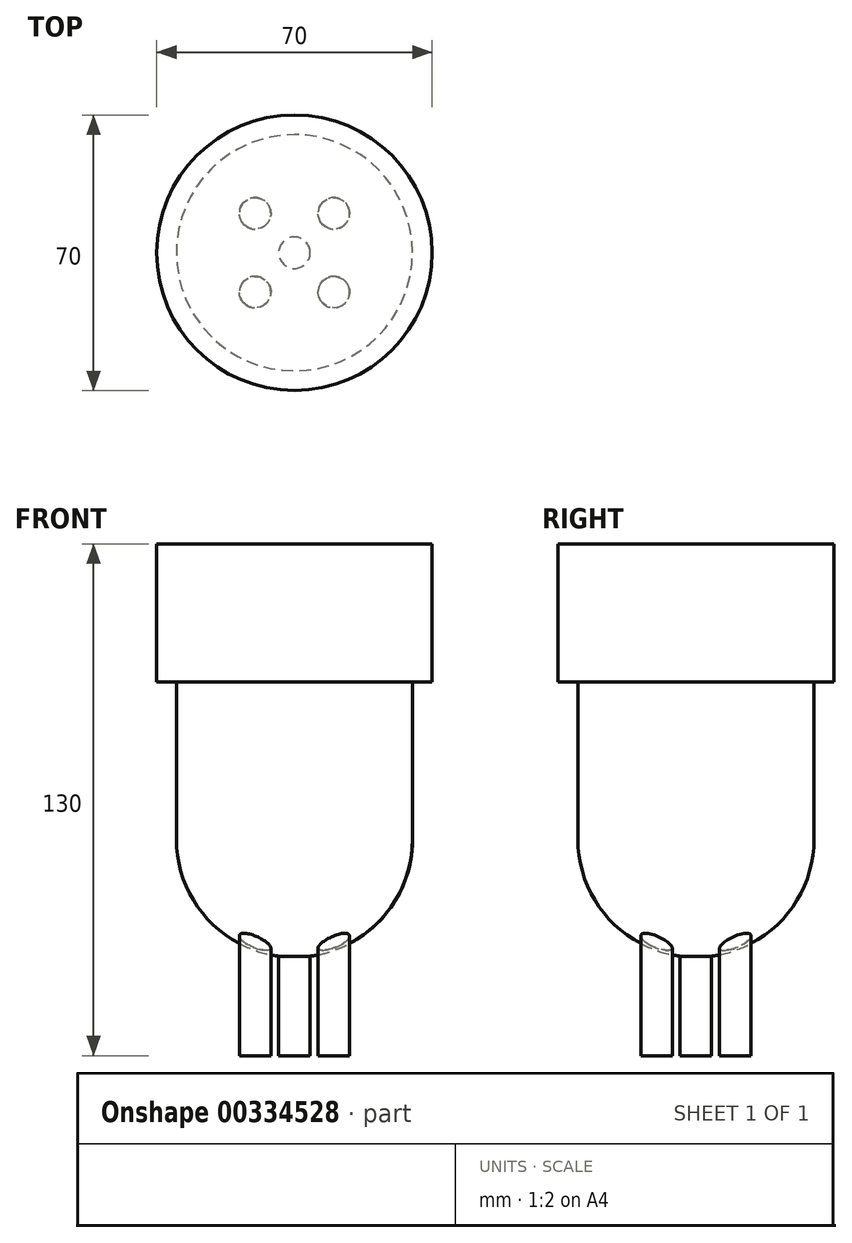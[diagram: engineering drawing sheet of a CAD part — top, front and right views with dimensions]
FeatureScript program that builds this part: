
annotation { "Feature Type Name" : "Feature", "Feature Type Description" : "" }
export const myFeature = defineFeature(function(context is Context, id is Id, definition is map)
    precondition{}
    {
        {
            var Q0;
            Q0=qCreatedBy(makeId("Front.planeOp"),FACE);
            var sketch = newSketch(context, id + "F0", { "sketchPlane" : qUnion([Q0])});
            skLineSegment(sketch, "E0.bottom", {"start": v(0, 70) * mm, "end": v(30, 70) * mm});
            skLineSegment(sketch, "E0.top", {"start": v(0, 30) * mm, "end": v(30, 30) * mm});
            skLineSegment(sketch, "E0.left", {"start": v(0, 70) * mm, "end": v(0, 30) * mm});
            skLineSegment(sketch, "E0.right", {"start": v(30, 70) * mm, "end": v(30, 30) * mm});
            skArc(sketch, "E1", {"start": v(30, 30) * mm, "mid": v(21.21, 8.79) * mm, "end": v(0, 0) * mm});
            skLineSegment(sketch, "E2", {"start": v(0, 30) * mm, "end": v(0, 0) * mm});
            skLineSegment(sketch, "E3.bottom", {"start": v(0, 70) * mm, "end": v(35, 70) * mm});
            skLineSegment(sketch, "E3.top", {"start": v(0, 105) * mm, "end": v(35, 105) * mm});
            skLineSegment(sketch, "E3.left", {"start": v(0, 70) * mm, "end": v(0, 105) * mm});
            skLineSegment(sketch, "E3.right", {"start": v(35, 70) * mm, "end": v(35, 105) * mm});
            skLineSegment(sketch, "E4", {"start": v(0, 70) * mm, "end": v(-15.84, 70) * mm, "construction": true});
            skLineSegment(sketch, "E5", {"start": v(0, 0) * mm, "end": v(0, -28.93) * mm, "construction": true});
            skSolve(sketch);
        }
        {
            var Q0;
            Q0=makeQuery(id+"F0.imprint","IMPRINT",FACE,{"disambiguationData":[TD([[makeQuery(id+"F0.imprint","IMPRINT",EDGE,{"derivedFrom":sQuery(id+"F0.wireOp",EDGE,"E3.top")}),-1.0]])]});
            var Q1;
            Q1=makeQuery(id+"F0.imprint","IMPRINT",FACE,{"disambiguationData":[TD([[makeQuery(id+"F0.imprint","IMPRINT",EDGE,{"derivedFrom":sQuery(id+"F0.wireOp",EDGE,"E0.top")}),1.0]])]});
            var Q2;
            Q2=makeQuery(id+"F0.imprint","IMPRINT",FACE,{"disambiguationData":[TD([[makeQuery(id+"F0.imprint","IMPRINT",EDGE,{"derivedFrom":sQuery(id+"F0.wireOp",EDGE,"E0.top")}),-1.0]])]});
            var Q3;
            Q3=sQuery(id+"F0.wireOp",EDGE,"E0.left");
            revolve(context, id + "F1", {"entities" : qUnion([Q0, Q1, Q2]), "axis" : qUnion([Q3]), "revolveType" : RevolveType.FULL});
        }
        {
            var Q0;
            Q0=qCreatedBy(makeId("Top.planeOp"),FACE);
            var sketch = newSketch(context, id + "F2", { "sketchPlane" : qUnion([Q0])});
            skLineSegment(sketch, "E6.bottom", {"start": v(10, 10) * mm, "end": v(-10, 10) * mm});
            skLineSegment(sketch, "E6.top", {"start": v(10, -10) * mm, "end": v(-10, -10) * mm});
            skLineSegment(sketch, "E6.left", {"start": v(10, 10) * mm, "end": v(10, -10) * mm});
            skLineSegment(sketch, "E6.right", {"start": v(-10, 10) * mm, "end": v(-10, -10) * mm});
            skPoint(sketch, "E6.middle", {"position": v(0, 0) * mm});
            skCircle(sketch, "E7", {"center": v(0, 0) * mm, "radius": 4 * mm});
            skCircle(sketch, "E8", {"center": v(10, -10) * mm, "radius": 4 * mm});
            skCircle(sketch, "E9", {"center": v(-10, -10) * mm, "radius": 4 * mm});
            skCircle(sketch, "E10", {"center": v(10, 10) * mm, "radius": 4 * mm});
            skCircle(sketch, "E11", {"center": v(-10, 10) * mm, "radius": 4 * mm});
            skSolve(sketch);
        }
        {
            var Q0;
            {var subQ0=sQuery(id+"F2.wireOp",EDGE,"E6.left");var subQ1=sQuery(id+"F2.wireOp",EDGE,"E6.bottom");var subQ2=makeQuery(id+"F2.imprint","INTERSECT",VERTEX,{"derivedFrom":[subQ1,subQ0]});Q0=makeQuery(id+"F2.imprint","IMPRINT",FACE,{"disambiguationData":[TD([[makeQuery(id+"F2.imprint","IMPRINT",EDGE,{"disambiguationData":[TD([[subQ2,-1.0]])],"derivedFrom":subQ1}),-1.0]])]});}
            var Q1;
            {var subQ0=sQuery(id+"F2.wireOp",EDGE,"E6.right");var subQ1=sQuery(id+"F2.wireOp",EDGE,"E6.bottom");var subQ2=makeQuery(id+"F2.imprint","INTERSECT",VERTEX,{"derivedFrom":[subQ1,subQ0]});Q1=makeQuery(id+"F2.imprint","IMPRINT",FACE,{"disambiguationData":[TD([[makeQuery(id+"F2.imprint","IMPRINT",EDGE,{"disambiguationData":[TD([[subQ2,1.0]])],"derivedFrom":subQ1}),-1.0]])]});}
            var Q2;
            {var subQ0=sQuery(id+"F2.wireOp",EDGE,"E6.left");var subQ1=sQuery(id+"F2.wireOp",EDGE,"E6.top");var subQ2=makeQuery(id+"F2.imprint","INTERSECT",VERTEX,{"derivedFrom":[subQ1,subQ0]});Q2=makeQuery(id+"F2.imprint","IMPRINT",FACE,{"disambiguationData":[TD([[makeQuery(id+"F2.imprint","IMPRINT",EDGE,{"disambiguationData":[TD([[subQ2,-1.0]])],"derivedFrom":subQ1}),1.0]])]});}
            var Q3;
            {var subQ0=sQuery(id+"F2.wireOp",EDGE,"E6.right");var subQ1=sQuery(id+"F2.wireOp",EDGE,"E6.top");var subQ2=makeQuery(id+"F2.imprint","INTERSECT",VERTEX,{"derivedFrom":[subQ1,subQ0]});Q3=makeQuery(id+"F2.imprint","IMPRINT",FACE,{"disambiguationData":[TD([[makeQuery(id+"F2.imprint","IMPRINT",EDGE,{"disambiguationData":[TD([[subQ2,1.0]])],"derivedFrom":subQ1}),1.0]])]});}
            var Q4;
            {var subQ0=sQuery(id+"F2.wireOp",EDGE,"E6.left");var subQ1=sQuery(id+"F2.wireOp",EDGE,"E6.bottom");var subQ2=makeQuery(id+"F2.imprint","INTERSECT",VERTEX,{"derivedFrom":[subQ1,subQ0]});Q4=makeQuery(id+"F2.imprint","IMPRINT",FACE,{"disambiguationData":[TD([[makeQuery(id+"F2.imprint","IMPRINT",EDGE,{"disambiguationData":[TD([[subQ2,-1.0]])],"derivedFrom":subQ1}),1.0]])]});}
            var Q5;
            {var subQ0=sQuery(id+"F2.wireOp",EDGE,"E6.right");var subQ1=sQuery(id+"F2.wireOp",EDGE,"E6.bottom");var subQ2=makeQuery(id+"F2.imprint","INTERSECT",VERTEX,{"derivedFrom":[subQ1,subQ0]});Q5=makeQuery(id+"F2.imprint","IMPRINT",FACE,{"disambiguationData":[TD([[makeQuery(id+"F2.imprint","IMPRINT",EDGE,{"disambiguationData":[TD([[subQ2,1.0]])],"derivedFrom":subQ1}),1.0]])]});}
            var Q6;
            {var subQ0=sQuery(id+"F2.wireOp",EDGE,"E6.left");var subQ1=sQuery(id+"F2.wireOp",EDGE,"E6.top");var subQ2=makeQuery(id+"F2.imprint","INTERSECT",VERTEX,{"derivedFrom":[subQ1,subQ0]});Q6=makeQuery(id+"F2.imprint","IMPRINT",FACE,{"disambiguationData":[TD([[makeQuery(id+"F2.imprint","IMPRINT",EDGE,{"disambiguationData":[TD([[subQ2,-1.0]])],"derivedFrom":subQ1}),-1.0]])]});}
            var Q7;
            {var subQ0=sQuery(id+"F2.wireOp",EDGE,"E6.right");var subQ1=sQuery(id+"F2.wireOp",EDGE,"E6.top");var subQ2=makeQuery(id+"F2.imprint","INTERSECT",VERTEX,{"derivedFrom":[subQ1,subQ0]});Q7=makeQuery(id+"F2.imprint","IMPRINT",FACE,{"disambiguationData":[TD([[makeQuery(id+"F2.imprint","IMPRINT",EDGE,{"disambiguationData":[TD([[subQ2,1.0]])],"derivedFrom":subQ1}),-1.0]])]});}
            var Q8;
            Q8=makeQuery(id+"F2.imprint","IMPRINT",FACE,{"disambiguationData":[TD([[makeQuery(id+"F2.imprint","IMPRINT",EDGE,{"derivedFrom":sQuery(id+"F2.wireOp",EDGE,"E7")}),1.0]])]});
            extrude(context, id + "F3", {"entities" : qUnion([Q0, Q1, Q2, Q3, Q4, Q5, Q6, Q7, Q8]), "operationType" : NewBodyOperationType.ADD, "depth" : 25 * mm});
        }
        {
            var Q0;
            Q0=makeQuery(id+"F3.opExtrude","CAP_FACE",FACE,{"disambiguationData":[OSD([sQuery(id+"F2.wireOp",EDGE,"E9")])],"isStart":true});
            var Q1;
            Q1=makeQuery(id+"F3.opExtrude","CAP_FACE",FACE,{"disambiguationData":[OSD([sQuery(id+"F2.wireOp",EDGE,"E7")])],"isStart":true});
            var Q2;
            Q2=makeQuery(id+"F3.opExtrude","CAP_FACE",FACE,{"disambiguationData":[OSD([sQuery(id+"F2.wireOp",EDGE,"E11")])],"isStart":true});
            var Q3;
            Q3=makeQuery(id+"F3.opExtrude","CAP_FACE",FACE,{"disambiguationData":[OSD([sQuery(id+"F2.wireOp",EDGE,"E8")])],"isStart":true});
            var Q4;
            Q4=makeQuery(id+"F3.opExtrude","CAP_FACE",FACE,{"disambiguationData":[OSD([sQuery(id+"F2.wireOp",EDGE,"E10")])],"isStart":true});
            extrude(context, id + "F4", {"entities" : qUnion([Q0, Q1, Q2, Q3, Q4]), "operationType" : NewBodyOperationType.ADD, "depth" : 25 * mm});
        }
    });
